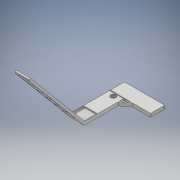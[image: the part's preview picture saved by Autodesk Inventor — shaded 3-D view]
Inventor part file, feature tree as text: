
AUTODESK INVENTOR PART (.ipt)
format: ipt  version: 2018 (Build 220112000, 112)  size: 280,064 bytes
history: native  units: mm
features: extrude x10, sketch x5, plane x2, mirror x2, other x1, projected_geometry x1
ambient origin geometry x8: Origin, YZ Plane, XZ Plane, XY Plane, X Axis, Y Axis, Z Axis, Center Point
bodies: Body1 (feature_tree)
feature tree (21):
  other  "Sólido1"
  sketch  "Boceto1"  dims[d0=51.0mm d1=27.5mm]
  extrude  "Extrusión1"  Depth=27.5mm
  extrude  "Extrusión2"  Depth=1.0mm
  plane  "Plano de trabajo1"
  mirror  "Simetría1"
  sketch  "Boceto2"  dims[d2=1.0mm d3=1.0mm]
  extrude  "Extrusión3"  Depth=27.5mm
  extrude  "Extrusión4"  Depth=1.0mm
  extrude  "Extrusión5"  Depth=2.5mm TaperAngle=0.0deg
  sketch  "Boceto4"  dims[d6=1.0mm d7=1.0mm]
  extrude  "Extrusión6"  Depth=10.0mm TaperAngle=0.0deg
  plane  "Plano de trabajo2"
  extrude  "Extrusión7"  Depth=1.5mm
  mirror  "Simetría2"
  sketch  "Boceto5"  dims[d8=80.0mm d9=2.5mm d10=0.0mm d11=0.96mm d12=0.0mm d13=1.5mm d14=4.42mm d15=0.0mm d16=12.0mm d17=9.0mm d18=4.0mm d19=20.0mm d20=6.92mm d21=0.0mm d22=25.5mm d23=0.0mm d26=6.981317mm d29=27.5mm d30=0.0mm d31=1.0mm d32=0.0mm d35=20.5mm d36=2.5mm d37=22.0mm d40=2.5mm d41=22.38mm d44=2.5mm d45=23.0mm d47=2.5mm d48=24.38mm d51=2.5mm d53=25.5mm d54=1.0mm d55=0.0mm d56=2.841mm d57=0.0mm d59=10.0mm d61=6.0mm d62=1.21mm d63=0.0mm]
  extrude  "Extrusión8"  Depth=4.42mm TaperAngle=0.0deg
  extrude  "Extrusión9"  Depth=10.0mm
  extrude  "Extrusión10"  Depth=10.0mm
  sketch  "Boceto3"  dims[d4=27.5mm d5=0.5mm]
  projected_geometry  "Contorno proyectado1"
